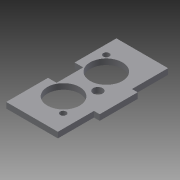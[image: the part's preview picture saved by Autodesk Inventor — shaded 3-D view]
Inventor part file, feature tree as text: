
AUTODESK INVENTOR PART (.ipt)
format: ipt  version: 2014 (Build 180170000, 170)  size: 101,376 bytes
history: native  units: mm
features: extrude x1, sketch x1
ambient origin geometry x8: Origin, YZ Plane, XZ Plane, XY Plane, X Axis, Y Axis, Z Axis, Center Point
bodies: Body1 (feature_tree)
feature tree (2):
  extrude  "Extrusion2"  Depth=58.0mm
  sketch  "Sketch1"  dims[d1=29.0mm d2=58.0mm d3=10.0mm d4=3.0mm d5=20.0mm d10=8.0mm d11=7.0mm d12=14.0mm d13=3.0mm d14=0.0mm]
